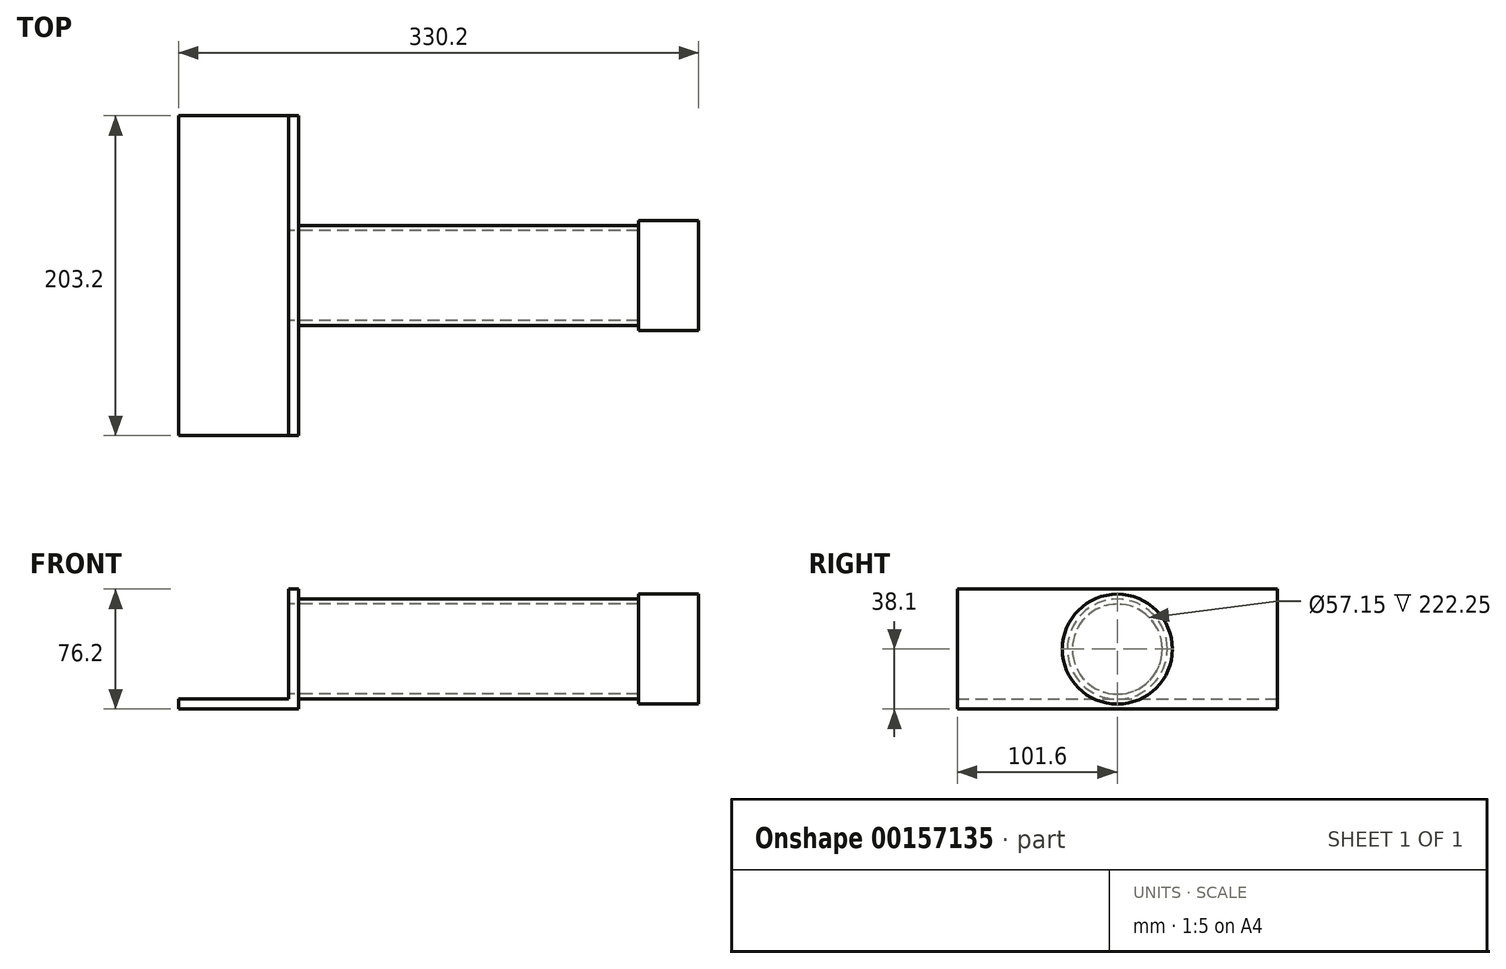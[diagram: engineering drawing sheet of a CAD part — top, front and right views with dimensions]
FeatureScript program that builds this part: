
annotation { "Feature Type Name" : "Feature", "Feature Type Description" : "" }
export const myFeature = defineFeature(function(context is Context, id is Id, definition is map)
    precondition{}
    {
        {
            var Q0;
            Q0=qCreatedBy(makeId("Front.planeOp"),FACE);
            var sketch = newSketch(context, id + "F0", { "sketchPlane" : qUnion([Q0])});
            skLineSegment(sketch, "E0", {"start": v(-76.2, 0) * mm, "end": v(0, 0) * mm});
            skLineSegment(sketch, "E1", {"start": v(0, 0) * mm, "end": v(0, 76.2) * mm});
            skLineSegment(sketch, "E2", {"start": v(0, 76.2) * mm, "end": v(-6.35, 76.2) * mm});
            skLineSegment(sketch, "E3", {"start": v(-6.35, 76.2) * mm, "end": v(-6.35, 6.35) * mm});
            skLineSegment(sketch, "E4", {"start": v(-6.35, 6.35) * mm, "end": v(-76.2, 6.35) * mm});
            skLineSegment(sketch, "E5", {"start": v(-76.2, 6.35) * mm, "end": v(-76.2, 0) * mm});
            skSolve(sketch);
        }
        {
            var Q0;
            Q0 = qSketchRegion(id + "F0", true);
            extrude(context, id + "F1", {"entities" : qUnion([Q0]), "depth" : 203.2 * mm});
        }
        {
            var Q0;
            Q0=makeQuery(id+"F1.opExtrude","SWEPT_FACE",FACE,{"disambiguationData":[OSD([sQuery(id+"F0.wireOp",EDGE,"E1")])]});
            var sketch = newSketch(context, id + "F2", { "sketchPlane" : qUnion([Q0])});
            skLineSegment(sketch, "E6", {"start": v(-101.6, 89.53) * mm, "end": v(-101.6, -38.47) * mm, "construction": true});
            skLineSegment(sketch, "E7", {"start": v(-221.41, 38.1) * mm, "end": v(31.75, 38.1) * mm, "construction": true});
            skCircle(sketch, "E8", {"center": v(-101.6, 38.1) * mm, "radius": 31.75 * mm});
            skCircle(sketch, "E9", {"center": v(-101.6, 38.1) * mm, "radius": 28.58 * mm});
            skSolve(sketch);
        }
        {
            var Q0;
            Q0 = qSketchRegion(id + "F2", true);
            extrude(context, id + "F3", {"entities" : qUnion([Q0]), "operationType" : NewBodyOperationType.ADD, "depth" : 254 * mm});
        }
        {
            var Q0;
            Q0=makeQuery(id+"F1.opExtrude","SWEPT_FACE",FACE,{"disambiguationData":[OSD([sQuery(id+"F0.wireOp",EDGE,"E3")])]});
            var sketch = newSketch(context, id + "F4", { "sketchPlane" : qUnion([Q0])});
            skLineSegment(sketch, "E10", {"start": v(101.6, 92.37) * mm, "end": v(101.6, -34.1) * mm, "construction": true});
            skLineSegment(sketch, "E11", {"start": v(-10.36, 38.1) * mm, "end": v(226.68, 38.1) * mm, "construction": true});
            skCircle(sketch, "E12", {"center": v(101.6, 38.1) * mm, "radius": 28.58 * mm});
            skSolve(sketch);
        }
        {
            var Q0;
            Q0 = qSketchRegion(id + "F4", true);
            var Q1;
            Q1 = qConstructionFilter(qBodyType(qCreatedBy(id + "F4" ,EDGE), BodyType.WIRE), ConstructionObject.NO);
            extrude(context, id + "F5", {"entities" : qUnion([Q0]), "operationType" : NewBodyOperationType.REMOVE, "surfaceEntities" : qUnion([Q1]), "endBound" : BoundingType.UP_TO_NEXT, "oppositeDirection" : true, "depth" : 25.4 * mm});
        }
        {
            var Q0;
            Q0=makeQuery(id+"F3.opExtrude","CAP_FACE",FACE,{"disambiguationData":[OSD([sQuery(id+"F2.wireOp",EDGE,"E8"),sQuery(id+"F2.wireOp",EDGE,"E9")])],"isStart":false});
            var sketch = newSketch(context, id + "F6", { "sketchPlane" : qUnion([Q0])});
            skCircle(sketch, "E13", {"center": v(-101.6, 38.1) * mm, "radius": 34.93 * mm});
            skSolve(sketch);
        }
        {
            var Q0;
            Q0 = qSketchRegion(id + "F6", true);
            extrude(context, id + "F7", {"entities" : qUnion([Q0]), "operationType" : NewBodyOperationType.ADD, "oppositeDirection" : true, "depth" : 38.1 * mm});
        }
    });
